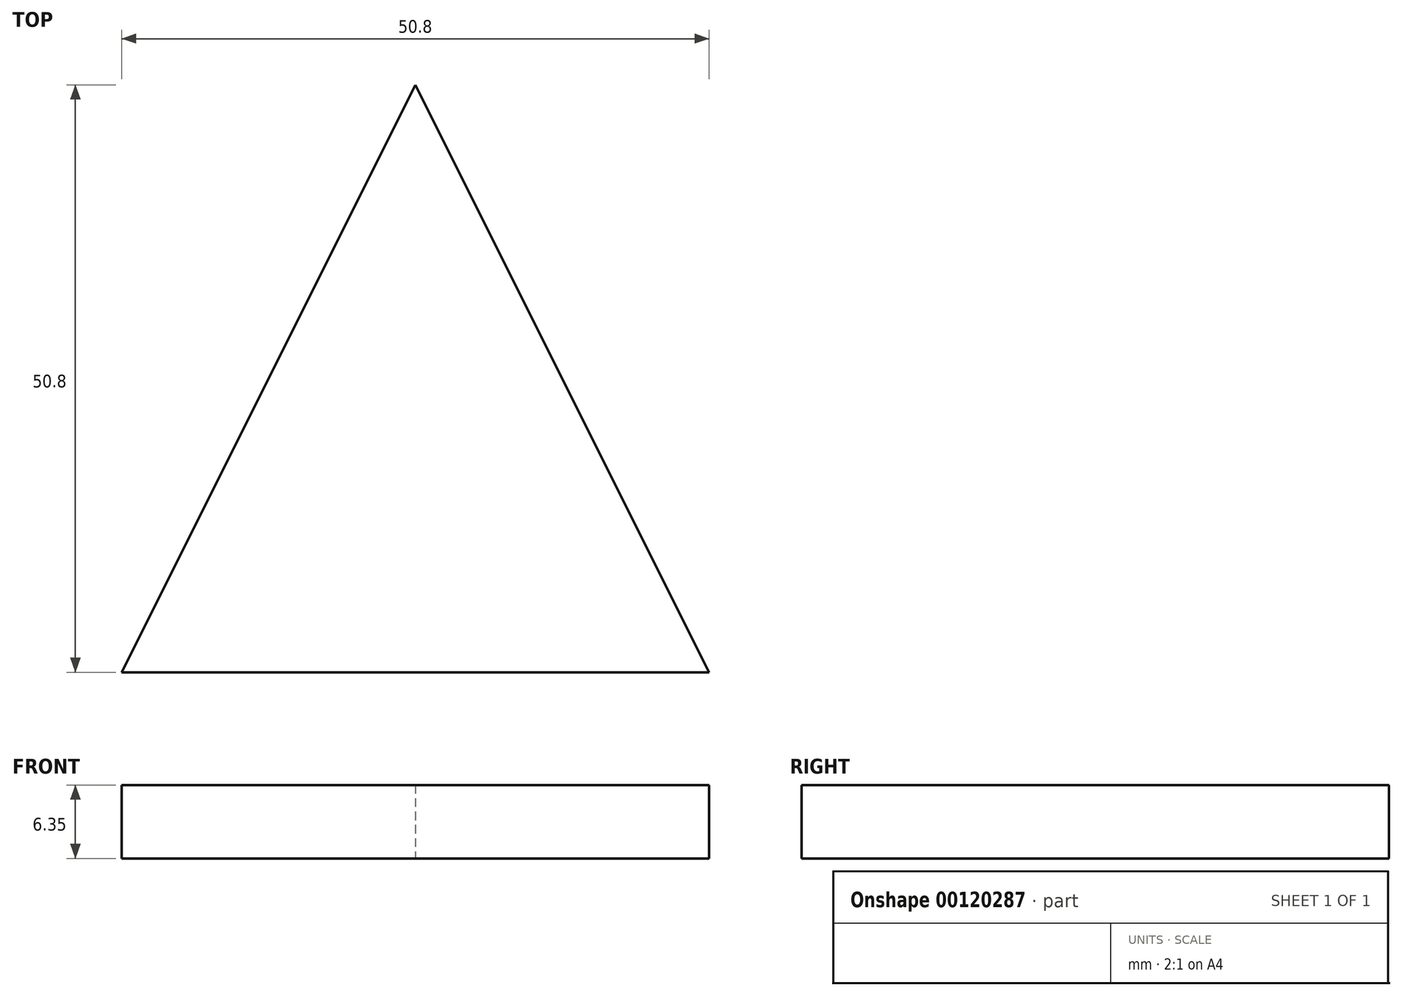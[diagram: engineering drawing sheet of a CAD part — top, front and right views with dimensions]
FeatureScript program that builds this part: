
annotation { "Feature Type Name" : "Feature", "Feature Type Description" : "" }
export const myFeature = defineFeature(function(context is Context, id is Id, definition is map)
    precondition{}
    {
        {
            var Q0;
            Q0=qCreatedBy(makeId("Top.planeOp"),FACE);
            var sketch = newSketch(context, id + "F0", { "sketchPlane" : qUnion([Q0])});
            skLineSegment(sketch, "E0", {"start": v(-25.4, 0) * mm, "end": v(25.4, 0) * mm});
            skLineSegment(sketch, "E1", {"start": v(0, 0) * mm, "end": v(0, 50.8) * mm, "construction": true});
            skLineSegment(sketch, "E2", {"start": v(-25.4, 0) * mm, "end": v(0, 50.8) * mm});
            skLineSegment(sketch, "E3", {"start": v(0, 50.8) * mm, "end": v(25.4, 0) * mm});
            skSolve(sketch);
        }
        {
            var Q0;
            Q0 = qSketchRegion(id + "F0", true);
            extrude(context, id + "F1", {"entities" : qUnion([Q0]), "depth" : 6.35 * mm});
        }
    });
